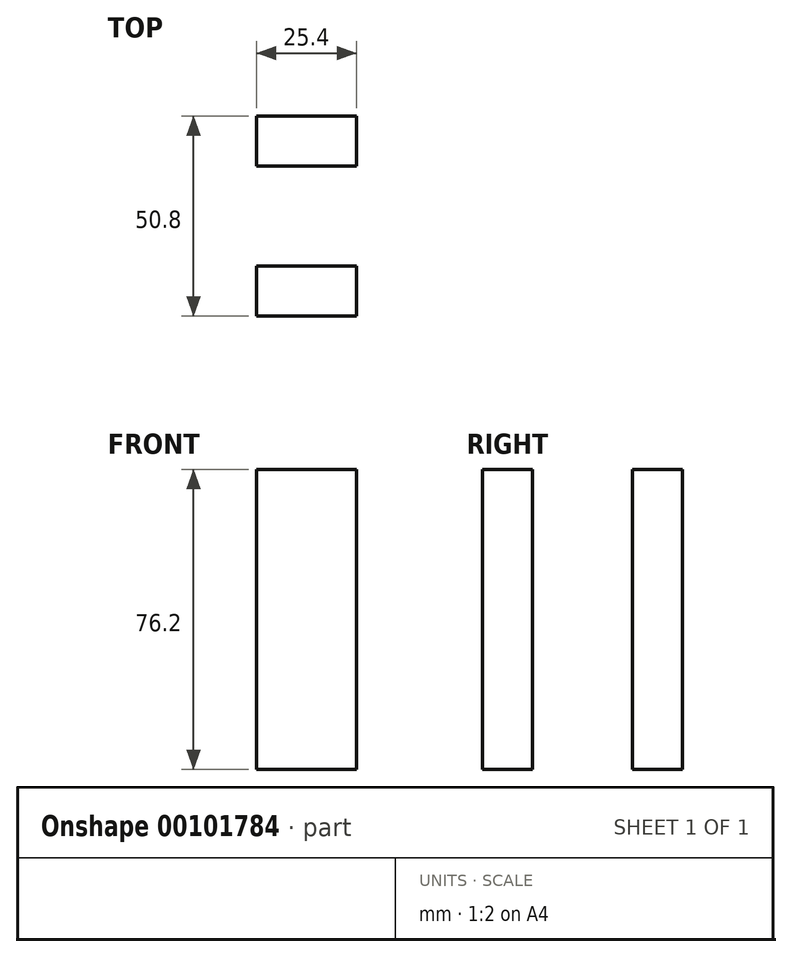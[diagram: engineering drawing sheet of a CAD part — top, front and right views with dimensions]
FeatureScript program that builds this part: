
annotation { "Feature Type Name" : "Feature", "Feature Type Description" : "" }
export const myFeature = defineFeature(function(context is Context, id is Id, definition is map)
    precondition{}
    {
        {
            var Q0;
            Q0=qCreatedBy(makeId("Front.planeOp"),FACE);
            var sketch = newSketch(context, id + "F0", { "sketchPlane" : qUnion([Q0])});
            skLineSegment(sketch, "E0.bottom", {"start": v(-25.4, 41.02) * mm, "end": v(0, 41.02) * mm});
            skLineSegment(sketch, "E0.top", {"start": v(-25.4, -35.18) * mm, "end": v(0, -35.18) * mm});
            skLineSegment(sketch, "E0.left", {"start": v(-25.4, 41.02) * mm, "end": v(-25.4, -35.18) * mm});
            skLineSegment(sketch, "E0.right", {"start": v(0, 41.02) * mm, "end": v(0, -35.18) * mm});
            skSolve(sketch);
        }
        {
            var Q0;
            Q0=makeQuery(id+"F0.imprint","IMPRINT",FACE,{"disambiguationData":[TD([[makeQuery(id+"F0.imprint","IMPRINT",EDGE,{"derivedFrom":sQuery(id+"F0.wireOp",EDGE,"E0.bottom")}),-1.0]])]});
            extrude(context, id + "F1", {"entities" : qUnion([Q0]), "depth" : 50.8 * mm});
        }
        {
            var Q0;
            Q0=makeQuery(id+"F1.opExtrude","SWEPT_FACE",FACE,{"disambiguationData":[OSD([sQuery(id+"F0.wireOp",EDGE,"E0.right")])]});
            var sketch = newSketch(context, id + "F2", { "sketchPlane" : qUnion([Q0])});
            skLineSegment(sketch, "E1", {"start": v(-38.1, 41.02) * mm, "end": v(-38.1, -35.18) * mm});
            skLineSegment(sketch, "E2", {"start": v(-12.7, 41.02) * mm, "end": v(-12.7, -35.18) * mm});
            skSolve(sketch);
        }
        {
            var Q0;
            {var subQ0=sQuery(id+"F2.wireOp",EDGE,"E1");Q0=makeQuery(id+"F2.imprint","IMPRINT",FACE,{"disambiguationData":[TD([[makeQuery(id+"F2.imprint","IMPRINT",EDGE,{"derivedFrom":subQ0}),1.0]])]});}
            extrude(context, id + "F3", {"entities" : qUnion([Q0]), "operationType" : NewBodyOperationType.REMOVE, "endBound" : BoundingType.THROUGH_ALL, "oppositeDirection" : true, "depth" : 25.4 * mm});
        }
    });
